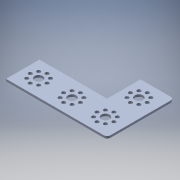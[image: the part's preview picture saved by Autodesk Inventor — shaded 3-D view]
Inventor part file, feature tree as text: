
AUTODESK INVENTOR PART (.ipt)
format: ipt  version: 2017 (Build 210142000, 142)  size: 322,560 bytes
history: native  units: in
note: dims shown in document units (in); Inventor stores cm internally (conversion verified against a paired STEP export)
features: other x2, split x2, sketch x2, fillet x1, imported_body x1, projected_geometry x1
ambient origin geometry x8: Origin, YZ Plane, XZ Plane, XY Plane, X Axis, Y Axis, Z Axis, Center Point
bodies: Body1 (feature_tree)
feature tree (9):
  other  "Flat Plate1"
  other  "Flat Plate"
  fillet  "Fillet1"  Radius=0.125in
  split  "Split1"
  split  "Split2"
  imported_body  "Base1"
  sketch  "Sketch1"  dims[d1=2.5in]
  projected_geometry  "Projected Loop1"
  sketch  "Sketch2"
